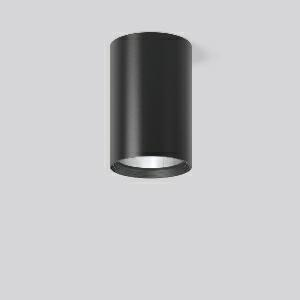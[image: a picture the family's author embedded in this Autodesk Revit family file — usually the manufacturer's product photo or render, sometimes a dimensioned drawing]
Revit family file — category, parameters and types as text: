
# Revit family: heledon_maxi_a_931217_003_1_2c0c
name_source: partatom
category: Lighting Fixtures
units: mm (PartAtom-declared; Revit-internal decimal feet)

## family parameters
Cut with Voids When Loaded = No
Host = Face
Light Source = No
Part Type = Normal
Room Calculation Point = No
Round Connector Dimension = Use Diameter
Shared = No

## types (1)
- HELEDON maxi A (1 x LED Modul 940, 3500 lm, 4000)
    Apparent Load = 25 VA
    Approval mark = CE
    CIE Flux Codes = 100 100 100 100 100
    Color Rendering = 92
    Color Temperature = 4000
    Default Elevation = 1800 mm
    Description = Series: HELEDON maxi
Cylindrical surface-mounted downlight. Housing: die-cast aluminium, powder-coated. Internal ceiling frame polycarbonate with bayonet mounting. Black plastic ring and recessed LED to prevent glare from the side. Optical assembly with reflector made of MIRO-Silver with 98% total light reflection for outstanding efficiency - can be changed without tools. Best colour rendering index Ra>90. Suitable for Ceiling mounting. Easy installation with a separate ceiling frame with bayonet mounting and plug connection. Driver integrated. Connected via plug-in connector. High quality converter without flickering and stroboscopic effect. The following accessories can be mounted without use of tools: interchangeable lenses, decorative glasses, honeycomb louvre, clear and frosted diffusers, white interchangeable plastic ring. 
Colour: deep black, matt (RAL 9005)
Diameter: 123 mm
Height: 183 mm
Lamp: LED
Socket: without socket
Colour temperature: 4000K
Colour rendering index (CRI): 92
System power: 25 W
Rated luminous flux: 3500 lm
Luminous efficiency: 140 lm/W
Control gear: Regulated power supply
Protection class: I
Type of protection: IP 20
    Height = 183 mm
    Lamp = 1 x LED Modul 940
    Lamp Light Flux = 3500 lm
    Lamp count = 1
    Length = 123 mm
    Lifetime = 50000 h
    Luminous efficacy = 140 lm/W
    Manufacturer = RZB
    ModVariant = No
    Model = 931217.003.1
    Mounting Place = Ceiling
    Mounting Type = Surface mounted
    Number of Poles = 1
    OnlyDefault = Yes
    Power Factor = 1
    Product Name = HELEDON maxi A
    Product group = Surface mounted downlights
    ProductGroupID = 302
    Protection Class = Protection class I
    Protection Degree = IP 20
    RLX_Detail_Level = 1
    RLX_Emergency_Light_Flux = 0 lm
    RLX_Emergency_Type = 0
    RLX_Emergency_Type_DB = No
    RlxData = <blob elided: 97497 chars, md5=57f41da9>
    Socket = socket
    Standby Power = 0 W
    System Light Flux = 3500 lm
    System Power = 25 W
    Type Comments = Product without accessories
    Type Image = 931192.003.jpg
    URL = http://relux.com
    VarID = ---
    Voltage = 230 V
    Voltage Range = 220-240 V
    Weight = 0.00 kg
    Width = 0 mm  [stored 0 ft]

note: [stored X ft] marks values corroborated as IEEE doubles in the binary element streams (Revit-internal decimal feet)

## geometry (parser evidence)
native form markers: Blend x4, Sweep x10
no freeform markers — native parametric forms only
